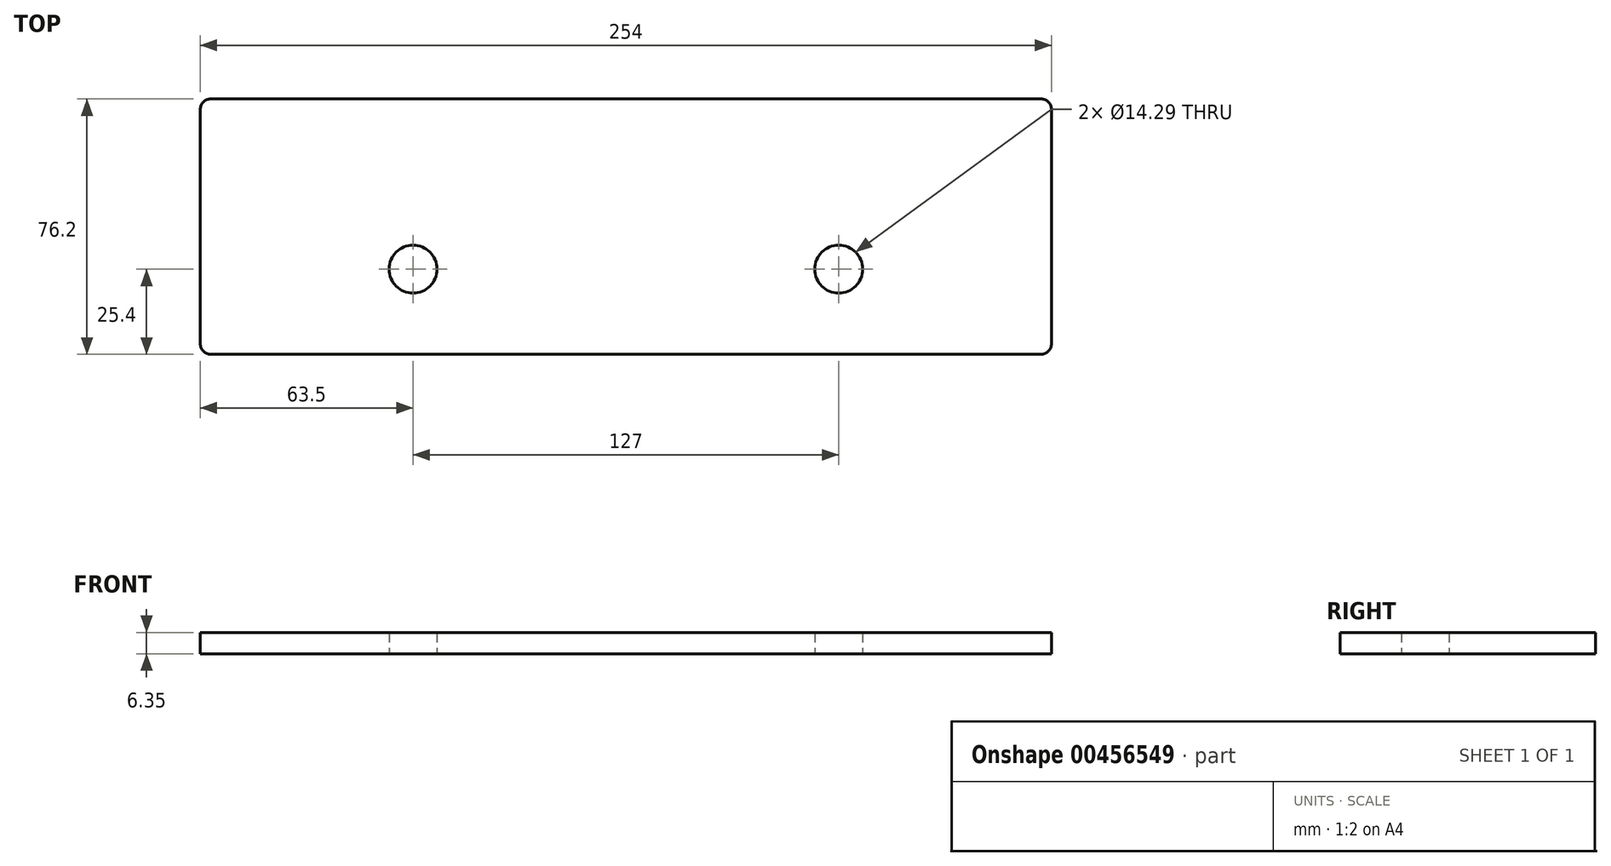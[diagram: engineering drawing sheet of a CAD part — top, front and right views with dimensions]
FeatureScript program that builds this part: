
annotation { "Feature Type Name" : "Feature", "Feature Type Description" : "" }
export const myFeature = defineFeature(function(context is Context, id is Id, definition is map)
    precondition{}
    {
        {
            var Q0;
            Q0=qCreatedBy(makeId("Top.planeOp"),FACE);
            var sketch = newSketch(context, id + "F0", { "sketchPlane" : qUnion([Q0])});
            skLineSegment(sketch, "E0", {"start": v(0, 0) * mm, "end": v(254, 0) * mm, "construction": true});
            skLineSegment(sketch, "E1", {"start": v(254, 0) * mm, "end": v(254, -76.2) * mm, "construction": true});
            skLineSegment(sketch, "E2.bottom", {"start": v(254, 0) * mm, "end": v(254, 0) * mm});
            skLineSegment(sketch, "E2.top", {"start": v(254, -76.2) * mm, "end": v(254, -76.2) * mm});
            skLineSegment(sketch, "E2.left", {"start": v(254, 0) * mm, "end": v(254, -76.2) * mm});
            skLineSegment(sketch, "E2.right", {"start": v(254, 0) * mm, "end": v(254, -76.2) * mm});
            skLineSegment(sketch, "E3.bottom", {"start": v(254, 0) * mm, "end": v(0, 0) * mm});
            skLineSegment(sketch, "E3.top", {"start": v(254, -76.2) * mm, "end": v(0, -76.2) * mm});
            skLineSegment(sketch, "E3.right", {"start": v(0, 0) * mm, "end": v(0, -76.2) * mm});
            skLineSegment(sketch, "E4", {"start": v(0, -76.2) * mm, "end": v(127, -76.2) * mm, "construction": true});
            skLineSegment(sketch, "E5", {"start": v(127, -76.2) * mm, "end": v(127, -50.8) * mm, "construction": true});
            skLineSegment(sketch, "E6", {"start": v(127, -50.8) * mm, "end": v(63.5, -50.8) * mm, "construction": true});
            skLineSegment(sketch, "E7", {"start": v(63.5, -50.8) * mm, "end": v(190.5, -50.8) * mm, "construction": true});
            skCircle(sketch, "E8", {"center": v(63.5, -50.8) * mm, "radius": 7.14 * mm});
            skCircle(sketch, "E9", {"center": v(190.5, -50.8) * mm, "radius": 7.14 * mm});
            skSolve(sketch);
        }
        {
            var Q0;
            Q0=makeQuery(id+"F0.imprint","IMPRINT",FACE,{"disambiguationData":[TD([[makeQuery(id+"F0.imprint","IMPRINT",EDGE,{"derivedFrom":sQuery(id+"F0.wireOp",EDGE,"E3.bottom")}),1.0]])]});
            extrude(context, id + "F1", {"entities" : qUnion([Q0]), "depth" : 6.35 * mm});
        }
        {
            var Q0;
            Q0=makeQuery(id+"F1.opExtrude","SWEPT_EDGE",EDGE,{"disambiguationData":[OSD([sQuery(id+"F0.wireOp",EDGE,"E3.top"),sQuery(id+"F0.wireOp",EDGE,"E2.left")])]});
            var Q1;
            Q1=makeQuery(id+"F1.opExtrude","SWEPT_EDGE",EDGE,{"disambiguationData":[OSD([sQuery(id+"F0.wireOp",EDGE,"E3.bottom"),sQuery(id+"F0.wireOp",EDGE,"E2.left")])]});
            var Q2;
            Q2=makeQuery(id+"F1.opExtrude","SWEPT_EDGE",EDGE,{"disambiguationData":[OSD([sQuery(id+"F0.wireOp",EDGE,"E3.bottom"),sQuery(id+"F0.wireOp",EDGE,"E3.right")])]});
            var Q3;
            Q3=makeQuery(id+"F1.opExtrude","SWEPT_EDGE",EDGE,{"disambiguationData":[OSD([sQuery(id+"F0.wireOp",EDGE,"E3.top"),sQuery(id+"F0.wireOp",EDGE,"E3.right")])]});
            fillet(context, id + "F2", {"entities" : qUnion([Q0, Q1, Q2, Q3]), "radius" : 3.17 * mm, "tangentPropagation" : true, "allowEdgeOverflow" : false});
        }
    });
